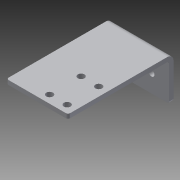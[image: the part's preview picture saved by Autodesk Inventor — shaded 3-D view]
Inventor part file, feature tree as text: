
AUTODESK INVENTOR PART (.ipt)
format: ipt  version: 2014 (Build 180170000, 170)  size: 130,048 bytes
history: native  units: in
note: dims shown in document units (in); Inventor stores cm internally (conversion verified against a paired STEP export)
features: sheet_metal_op x4, sketch x3, other x2, fillet x1, extrude x1
ambient origin geometry x8: Origin, YZ Plane, XZ Plane, XY Plane, X Axis, Y Axis, Z Axis, Center Point
bodies: Solid1 (feature_tree)
feature tree (11):
  sheet_metal_op  "Face1"
  sheet_metal_op  "Flange1"
  fillet  "Fillet1"  Radius=1.75in
  extrude  "Extrusion1"  Depth=0.163in
  sketch  "Sketch1"  dims[d1=1.0in d2=0.163in]
  other  "Plate1"
  sketch  "Sketch2"  dims[d4=0.7874in d6=1.0in d7=0.3937in d9=1.0in]
  other  "Plate2"
  sheet_metal_op  "Bend1"
  sheet_metal_op  "Corner1"
  sketch  "Sketch3"  dims[d11=0.125in d12=0.125in d13=0.0625in d14=0.25in d15=0.125in d16=3.0in d17=90.0deg d18=0.05in d19=0.5in d20=0.125in d21=0.125in d22=0.0625in d23=1.35in d24=0.75in d27=0.19in d28=0.125in d29=0.2265in d30=1.0in d31=0.0in d34=0.25in d35=0.875in]
